# Revit family: P210876JX-009_JUGFL242HL_JUGFR242HL
name_source: partatom
category: Specialty Equipment
units: mm (PartAtom-declared; Revit-internal decimal feet)

## family parameters
Always vertical = Yes
Cut with Voids When Loaded = No
Enable Cutting in Views = No
Maintain Annotation Orientation = No
Part Type = Normal
Room Calculation Point = No
Round Connector Dimension = Use Diameter
Shared = No
Work Plane-Based = No

## types (1)
- JUGFL242HL
    Amps = 0 A
    Back Panel Material = ARCAT - Metal - Aluminum
    Body Material = ARCAT - Metal - Steel - Black
    Clearance Material = ARCAT - Clearance
    Default Elevation = 0"
    Depth = 23 13/16"
    Description = RISE™ 24"  Under Counter Glass Door Refrigerator, Left Swing
Réfrigérateur à porte en verre sous le comptoir, charnière à gauche, RISE™, 24 po
    Dimension Guide = https://whirlpool.com
https://whirlpool.com
    Door Material = ARCAT - Metal - Steel - Stainless
    Energy Guide = https://www.whirlpool.com
https://www.whirlpool.com
    Family Name = Undercounter Specialty
    Feature 1 = UV-Resistant Low-E Thermal Glass
Porte en verre thermique à faible émissivité résistant aux UV
    Feature 2 = Daring Obsidian Interior
Daring Obsidian Interior
    Feature 3 = Emotive Controls
Emotive Controls
    Glass Material = ARCAT - Glass - Gray
    Handle Material = ARCAT - Metal - Steel - Grey
    Height = 34 1/8"
    Hinge Material = ARCAT - Plastic - Black
    Leg Material = ARCAT - Plastic - Black
    Manufacturer = JennAir
    Model = JUGFL242HL
    Screw Material = ARCAT - Metal - Steel - Stainless
    Tray Material = ARCAT - Metal - Steel - Stainless
    Voltage = 0 V
    Width = 23 7/8"

## geometry (parser evidence)
native form markers: Sweep x3
no freeform markers — native parametric forms only
